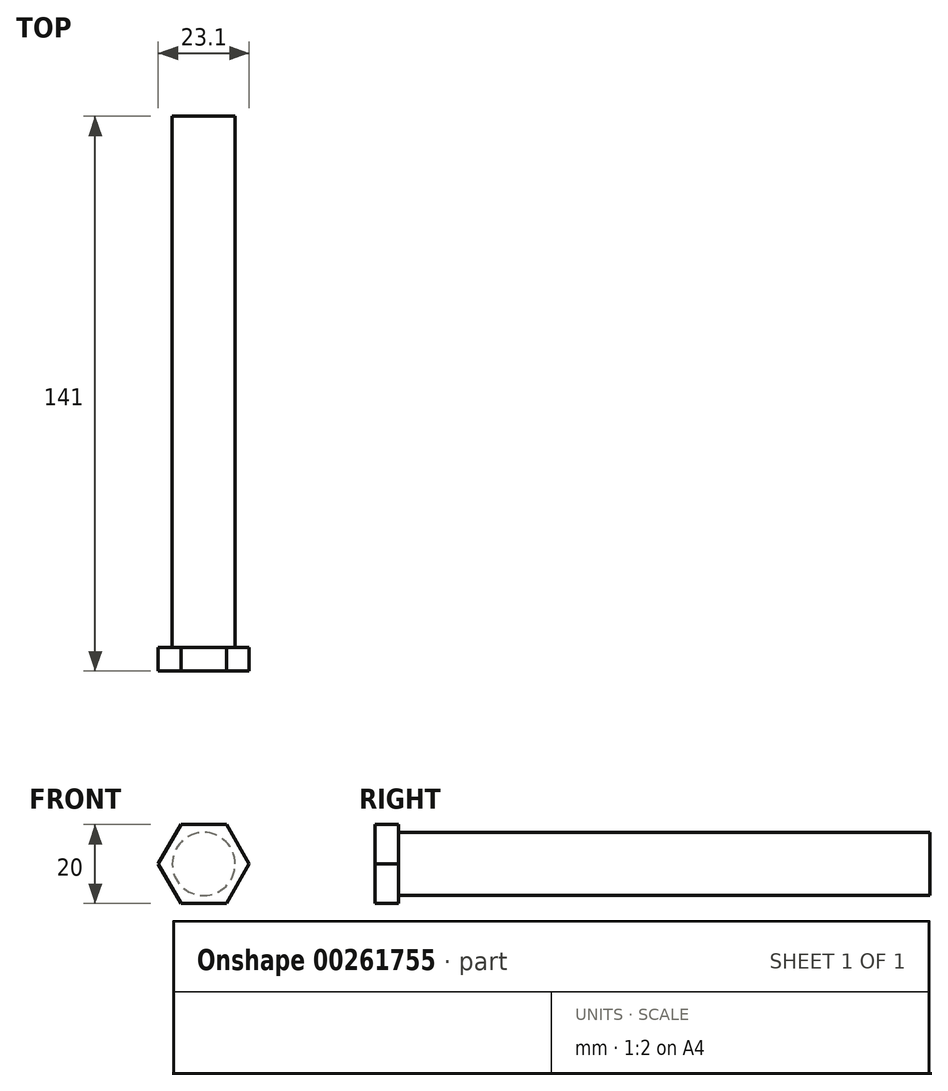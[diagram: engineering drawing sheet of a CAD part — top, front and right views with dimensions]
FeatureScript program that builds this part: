
annotation { "Feature Type Name" : "Feature", "Feature Type Description" : "" }
export const myFeature = defineFeature(function(context is Context, id is Id, definition is map)
    precondition{}
    {
        {
            var Q0;
            Q0=qCreatedBy(makeId("Front.planeOp"),FACE);
            var sketch = newSketch(context, id + "F0", { "sketchPlane" : qUnion([Q0])});
            skCircle(sketch, "E0", {"center": v(0, 0) * mm, "radius": 8 * mm});
            skSolve(sketch);
        }
        {
            var Q0;
            Q0=makeQuery(id+"F0.imprint","IMPRINT",FACE,{"disambiguationData":[TD([[makeQuery(id+"F0.imprint","IMPRINT",EDGE,{"derivedFrom":sQuery(id+"F0.wireOp",EDGE,"E0")}),1.0]])]});
            extrude(context, id + "F1", {"entities" : qUnion([Q0]), "oppositeDirection" : true, "depth" : 135 * mm});
        }
        {
            var Q0;
            Q0=makeQuery(id+"F1.opExtrude","CAP_FACE",FACE,{"disambiguationData":[OSD([sQuery(id+"F0.wireOp",EDGE,"E0")])],"isStart":true});
            var sketch = newSketch(context, id + "F2", { "sketchPlane" : qUnion([Q0])});
            skCircle(sketch, "E1.cCircle", {"center": v(0, 0) * mm, "radius": 10 * mm, "construction": true});
            skLineSegment(sketch, "E1.0", {"start": v(-5.77, 10) * mm, "end": v(5.77, 10) * mm});
            skLineSegment(sketch, "E1.1", {"start": v(5.77, 10) * mm, "end": v(11.55, 0) * mm});
            skLineSegment(sketch, "E1.2", {"start": v(11.55, 0) * mm, "end": v(5.77, -10) * mm});
            skLineSegment(sketch, "E1.3", {"start": v(5.77, -10) * mm, "end": v(-5.77, -10) * mm});
            skLineSegment(sketch, "E1.4", {"start": v(-5.77, -10) * mm, "end": v(-11.55, 0) * mm});
            skLineSegment(sketch, "E1.5", {"start": v(-11.55, 0) * mm, "end": v(-5.77, 10) * mm});
            skPoint(sketch, "E1.0.midPoint", {"position": v(0, 10) * mm});
            skSolve(sketch);
        }
        {
            var Q0;
            Q0=makeQuery(id+"F2.imprint","IMPRINT",FACE,{"disambiguationData":[TD([[makeQuery(id+"F2.imprint","IMPRINT",EDGE,{"derivedFrom":sQuery(id+"F2.wireOp",EDGE,"E1.0")}),-1.0]])]});
            var Q1;
            Q1=makeQuery(id+"F2.imprint","IMPRINT",FACE,{"disambiguationData":[TD([[makeQuery(id+"F2.imprint","IMPRINT",EDGE,{"derivedFrom":makeQuery(id+"F1.opExtrude","CAP_EDGE",EDGE,{"disambiguationData":[OSD([sQuery(id+"F0.wireOp",EDGE,"E0")])],"isStart":true})}),1.0]])]});
            extrude(context, id + "F3", {"entities" : qUnion([Q0, Q1]), "operationType" : NewBodyOperationType.ADD, "depth" : 6 * mm});
        }
    });
